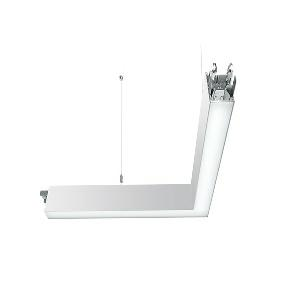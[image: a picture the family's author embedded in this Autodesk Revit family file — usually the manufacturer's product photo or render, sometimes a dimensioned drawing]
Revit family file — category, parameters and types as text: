
# Revit family: dotoo_line_-_dlp_1500_840_d_ll_mid_00807692_86ba
name_source: partatom
category: Lighting Fixtures
units: mm (PartAtom-declared; Revit-internal decimal feet)

## family parameters
Cut with Voids When Loaded = No
Host = Face
Light Source = No
Part Type = Normal
Room Calculation Point = No
Round Connector Dimension = Use Diameter
Shared = No

## types (1)
- DOTOO.line - DLP 1500/840/D/LL MID (1 x LED, 1350 lm, 4000K)
    Apparent Load = 13 VA
    Approval mark = CE
    CIE Flux Codes = 67 91 98 100 100
    Color Rendering = 80-89
    Color Temperature = 4000K
    Control Gear = Electronic ballast
    Default Elevation = 1800 mm
    Description = DLP 1500/840/D|Suspended luminaire|light source: LED|connected load: 220-240 V, 50/60 Hz|Power consumption: approx. 13 W|standby: approx. 0,20|luminous flux: 1350 lm|luminous efficacy: 103 lm/W|light distribution: Direct|direct ratio: approx. 100 %|colour temperature: Cold white, ca. 4000 K|color rendering index (CRI): >= 80|chromaticity tolerance:  3 SDCM|System of protection: IP 40|technology: Continuously dimmable|luminaire body|material: Sectional aluminium|colour: White|lamp cover: Acrylic (PMMA), Clear|Fastening: Steel cable 0.3 - 0.7 m|glare control: Prism aperture|luminance(L65): <= 3000 cd/m|unified glare rating(4H 8H): <=  19|special features: DALI Load 1x, TouchDIM - dimming via standard switch, Through-wired, up to 18 m on one mains connection, Flicker-free, Continous light without dark z, 90░ rerouting on the left side, Suitable as emergency lighting, Mechanical and electrical connection of the individual modules without tools|
    Frequency = 50 Hz
    Height = 110 mm
    Lamp = 1 x LED
    Lamp Light Flux = 1350 lm
    Lamp count = 1
    Length = 600 mm
    Luminous efficacy = 104 lm/W
    Manufacturer = Waldmann
    ModVariant = No
    Model = 00807692
    Mounting Place = Ceiling
    Mounting Type = Pendant
    Number of Poles = 1
    OnlyDefault = Yes
    Power Factor = 1
    Product Name = DOTOO.line - DLP 1500/840/D/LL MID
    Product group = Suspended luminaire
    ProductGroupID = 9
    Protection Class = Protection class I
    Protection Degree = IP 40
    RLX_Detail_Level = 1
    RLX_Emergency_Light_Flux = 0 lm
    RLX_Emergency_Type = 0
    RLX_Emergency_Type_DB = No
    RlxData = <blob elided: 21129 chars, md5=97f41da8>
    Socket = socket
    Standby Power = 0 W
    System Light Flux = 1350 lm
    System Power = 13 W
    Type Comments = Product without accessories
    Type Image = ilp_dlp_ll_ws.jpg
    URL = http://relux.com
    VarID = ---
    Voltage = 230 V
    Voltage Range = 220-240 V
    Weight = 0.00 kg
    Width = 600 mm

## geometry (parser evidence)
native form markers: Blend x4, Sweep x13
no freeform markers — native parametric forms only
